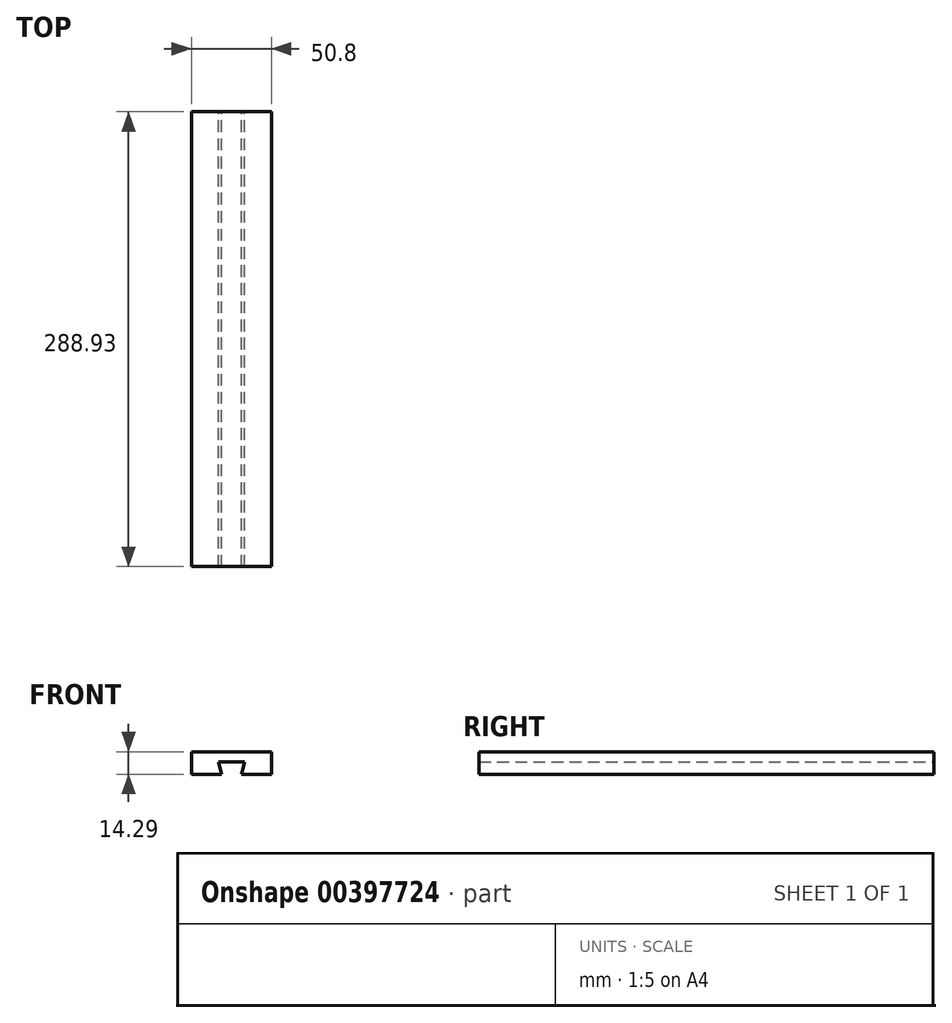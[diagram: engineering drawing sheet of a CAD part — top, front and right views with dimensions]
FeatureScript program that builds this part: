
annotation { "Feature Type Name" : "Feature", "Feature Type Description" : "" }
export const myFeature = defineFeature(function(context is Context, id is Id, definition is map)
    precondition{}
    {
        {
            var Q0;
            Q0=qCreatedBy(makeId("Front.planeOp"),FACE);
            var sketch = newSketch(context, id + "F0", { "sketchPlane" : qUnion([Q0])});
            skLineSegment(sketch, "E0.bottom", {"start": v(0, 0) * mm, "end": v(50.8, 0) * mm, "construction": true});
            skLineSegment(sketch, "E0.top", {"start": v(0, 19.05) * mm, "end": v(50.8, 19.05) * mm});
            skLineSegment(sketch, "E0.left", {"start": v(0, 0) * mm, "end": v(0, 4.76) * mm, "construction": true});
            skLineSegment(sketch, "E0.right", {"start": v(50.8, 0) * mm, "end": v(50.8, 4.76) * mm, "construction": true});
            skLineSegment(sketch, "E1", {"start": v(0, 4.76) * mm, "end": v(19.05, 4.76) * mm});
            skLineSegment(sketch, "E2", {"start": v(0, 4.76) * mm, "end": v(0, 19.05) * mm});
            skLineSegment(sketch, "E3", {"start": v(50.8, 4.76) * mm, "end": v(50.8, 19.05) * mm});
            skLineSegment(sketch, "E4", {"start": v(17.07, 12.7) * mm, "end": v(33.73, 12.7) * mm});
            skLineSegment(sketch, "E5", {"start": v(33.73, 12.7) * mm, "end": v(31.75, 4.76) * mm});
            skLineSegment(sketch, "E6", {"start": v(17.07, 12.7) * mm, "end": v(19.05, 4.76) * mm});
            skLineSegment(sketch, "E7.trimOffspring", {"start": v(31.75, 4.76) * mm, "end": v(50.8, 4.76) * mm});
            skSolve(sketch);
        }
        {
            var Q0;
            Q0=makeQuery(id+"F0.imprint","IMPRINT",FACE,{"disambiguationData":[TD([[makeQuery(id+"F0.imprint","IMPRINT",EDGE,{"derivedFrom":sQuery(id+"F0.wireOp",EDGE,"E0.top")}),-1.0]])]});
            extrude(context, id + "F1", {"entities" : qUnion([Q0]), "depth" : 288.93 * mm});
        }
    });
